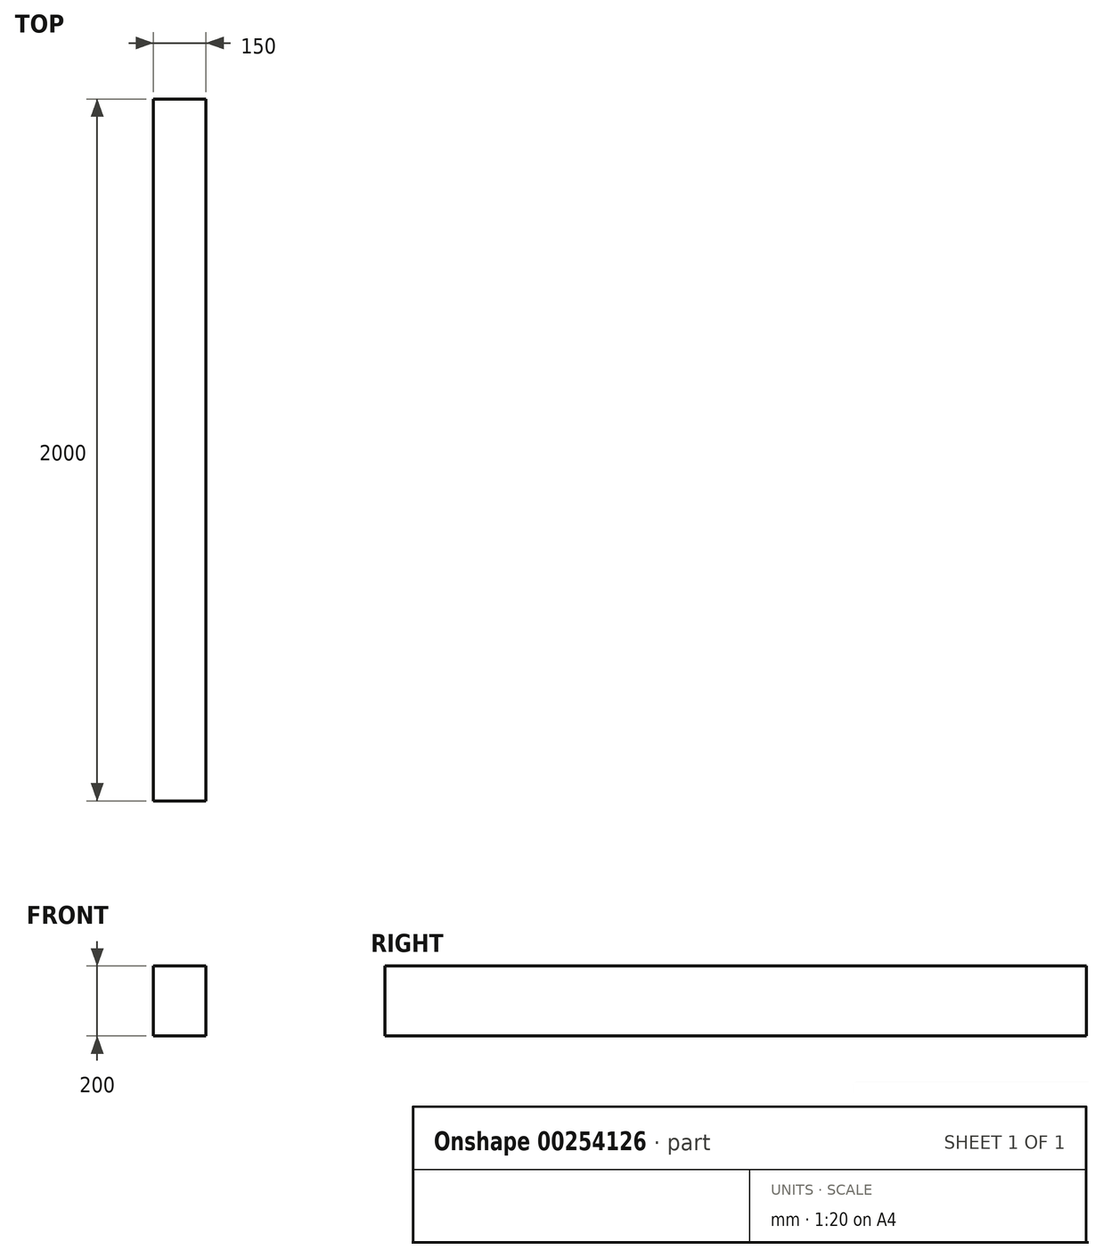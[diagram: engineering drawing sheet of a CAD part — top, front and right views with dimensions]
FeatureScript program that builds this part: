
annotation { "Feature Type Name" : "Feature", "Feature Type Description" : "" }
export const myFeature = defineFeature(function(context is Context, id is Id, definition is map)
    precondition{}
    {
        {
            var Q0;
            Q0=qCreatedBy(makeId("Front.planeOp"),FACE);
            var sketch = newSketch(context, id + "F0", { "sketchPlane" : qUnion([Q0])});
            skLineSegment(sketch, "E0.bottom", {"start": v(75, -100) * mm, "end": v(-75, -100) * mm});
            skLineSegment(sketch, "E0.top", {"start": v(75, 100) * mm, "end": v(-75, 100) * mm});
            skLineSegment(sketch, "E0.left", {"start": v(75, -100) * mm, "end": v(75, 100) * mm});
            skLineSegment(sketch, "E0.right", {"start": v(-75, -100) * mm, "end": v(-75, 100) * mm});
            skPoint(sketch, "E0.middle", {"position": v(0, 0) * mm});
            skSolve(sketch);
        }
        {
            var Q0;
            Q0 = qSketchRegion(id + "F0", true);
            extrude(context, id + "F1", {"entities" : qUnion([Q0]), "endBound" : BoundingType.SYMMETRIC, "depth" : 2000 * mm});
        }
    });
